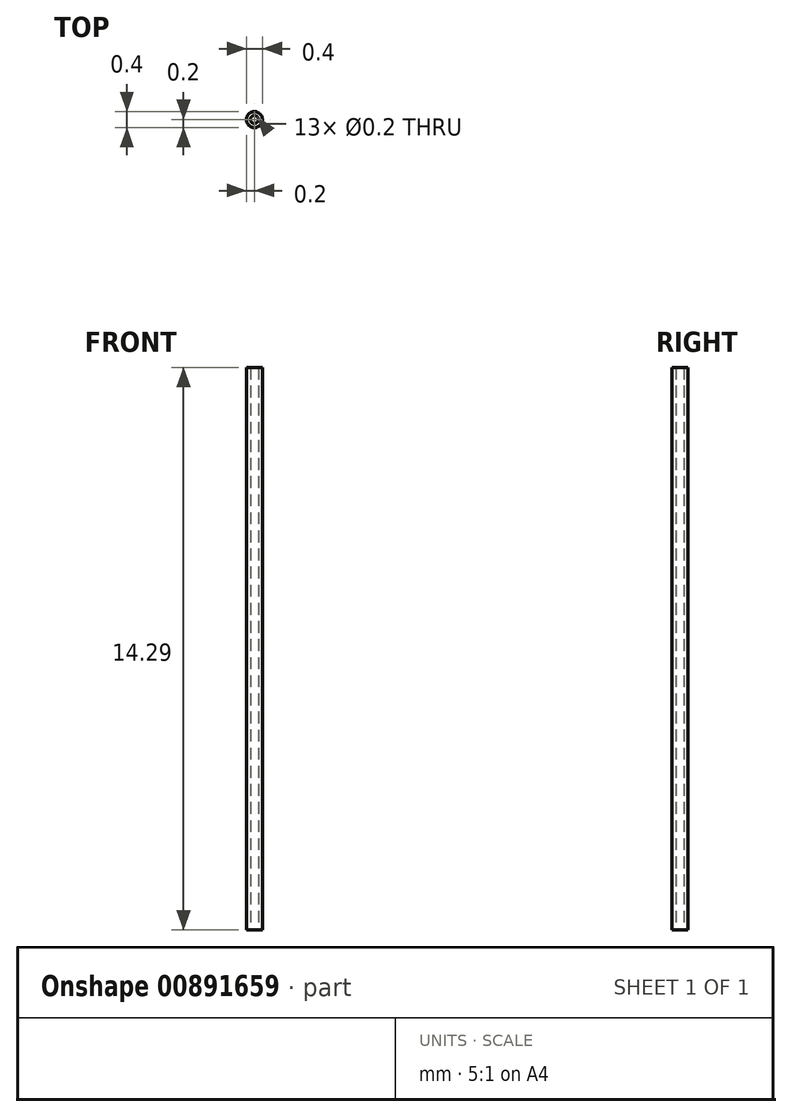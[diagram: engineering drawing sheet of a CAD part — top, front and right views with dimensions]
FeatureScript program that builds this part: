
annotation { "Feature Type Name" : "Feature", "Feature Type Description" : "" }
export const myFeature = defineFeature(function(context is Context, id is Id, definition is map)
    precondition{}
    {
        {
            var Q0;
            Q0=qCreatedBy(makeId("Top.planeOp"),FACE);
            var sketch = newSketch(context, id + "F0", { "sketchPlane" : qUnion([Q0])});
            skCircle(sketch, "E0", {"center": v(0, 0) * mm, "radius": 0.1 * mm});
            skCircle(sketch, "E1", {"center": v(0, 0) * mm, "radius": 0.2 * mm});
            skSolve(sketch);
        }
        {
            var Q0;
            Q0=makeQuery(id+"F0.imprint","IMPRINT",FACE,{"disambiguationData":[TD([[makeQuery(id+"F0.imprint","IMPRINT",EDGE,{"derivedFrom":sQuery(id+"F0.wireOp",EDGE,"E0")}),-1.0]])]});
            extrude(context, id + "F1", {"entities" : qUnion([Q0]), "depth" : 14.29 * mm, "offsetDistance" : 25.4 * mm});
        }
    });
